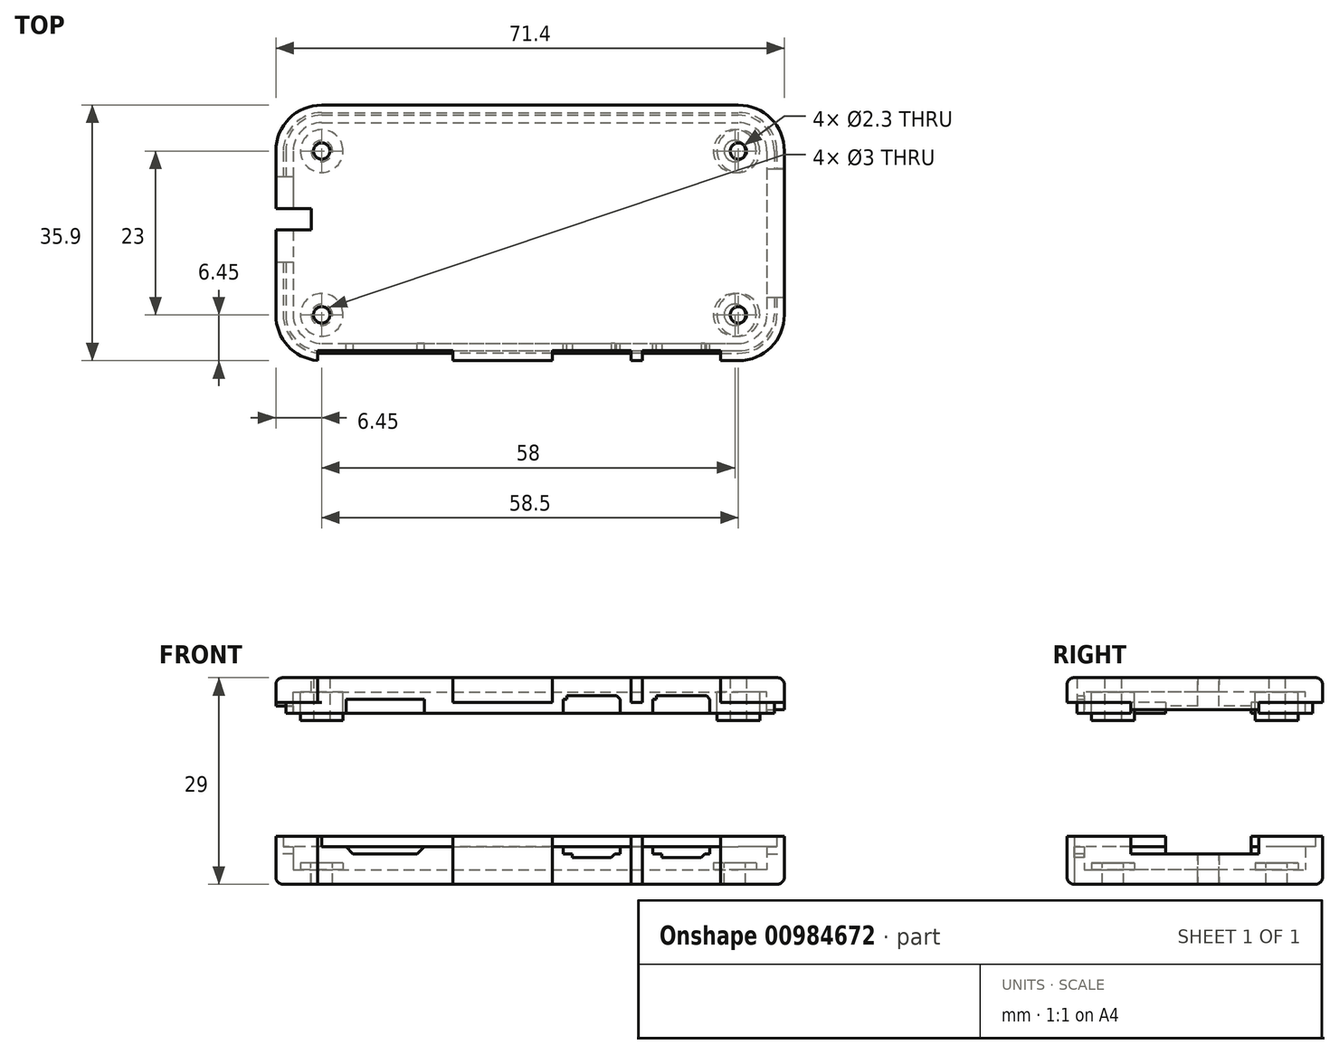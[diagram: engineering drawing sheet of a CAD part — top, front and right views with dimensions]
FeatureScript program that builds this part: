
annotation { "Feature Type Name" : "Feature", "Feature Type Description" : "" }
export const myFeature = defineFeature(function(context is Context, id is Id, definition is map)
    precondition{}
    {
        {
            var Q0;
            Q0=qCreatedBy(makeId("Top.planeOp"),FACE);
            var sketch = newSketch(context, id + "F0", { "sketchPlane" : qUnion([Q0])});
            skLineSegment(sketch, "E0.bottom", {"start": v(62, 30) * mm, "end": v(3, 30) * mm, "construction": true});
            skLineSegment(sketch, "E0.top", {"start": v(62, 0) * mm, "end": v(3, 0) * mm, "construction": true});
            skLineSegment(sketch, "E0.left", {"start": v(65, 27) * mm, "end": v(65, 3) * mm, "construction": true});
            skLineSegment(sketch, "E0.right", {"start": v(0, 27) * mm, "end": v(0, 3) * mm, "construction": true});
            skPoint(sketch, "E0.middle", {"position": v(32.5, 15) * mm});
            skLineSegment(sketch, "E1.bottom", {"start": v(61.5, 3.5) * mm, "end": v(3.5, 3.5) * mm, "construction": true});
            skLineSegment(sketch, "E1.top", {"start": v(61.5, 26.5) * mm, "end": v(3.5, 26.5) * mm, "construction": true});
            skLineSegment(sketch, "E1.left", {"start": v(61.5, 3.5) * mm, "end": v(61.5, 26.5) * mm, "construction": true});
            skLineSegment(sketch, "E1.right", {"start": v(3.5, 3.5) * mm, "end": v(3.5, 26.5) * mm, "construction": true});
            skPoint(sketch, "E2", {"position": v(0, 16.9) * mm});
            skPoint(sketch, "E3", {"position": v(12.4, 0) * mm});
            skPoint(sketch, "E4", {"position": v(41.4, 0) * mm});
            skPoint(sketch, "E5", {"position": v(54, 0) * mm});
            skPoint(sketch, "E6", {"position": v(65, 15) * mm});
            skPoint(sketch, "E7", {"position": v(32.5, 26.5) * mm});
            skLineSegment(sketch, "E8.bottom", {"start": v(58, 24) * mm, "end": v(7, 24) * mm, "construction": true});
            skLineSegment(sketch, "E8.top", {"start": v(58, 29) * mm, "end": v(7, 29) * mm, "construction": true});
            skLineSegment(sketch, "E8.left", {"start": v(58, 24) * mm, "end": v(58, 29) * mm, "construction": true});
            skLineSegment(sketch, "E8.right", {"start": v(7, 24) * mm, "end": v(7, 29) * mm, "construction": true});
            skLineSegment(sketch, "E9.bottom", {"start": v(50, 4) * mm, "end": v(58, 4) * mm, "construction": true});
            skLineSegment(sketch, "E9.top", {"start": v(50, -1.5) * mm, "end": v(58, -1.5) * mm, "construction": true});
            skLineSegment(sketch, "E9.left", {"start": v(50, 4) * mm, "end": v(50, -1.5) * mm, "construction": true});
            skLineSegment(sketch, "E9.right", {"start": v(58, 4) * mm, "end": v(58, -1.5) * mm, "construction": true});
            skLineSegment(sketch, "E10.bottom", {"start": v(37.4, 4) * mm, "end": v(45.4, 4) * mm, "construction": true});
            skLineSegment(sketch, "E10.top", {"start": v(37.4, -1.5) * mm, "end": v(45.4, -1.5) * mm, "construction": true});
            skLineSegment(sketch, "E10.left", {"start": v(37.4, 4) * mm, "end": v(37.4, -1.5) * mm, "construction": true});
            skLineSegment(sketch, "E10.right", {"start": v(45.4, 4) * mm, "end": v(45.4, -1.5) * mm, "construction": true});
            skLineSegment(sketch, "E11.bottom", {"start": v(6.9, 6.5) * mm, "end": v(17.9, 6.5) * mm, "construction": true});
            skLineSegment(sketch, "E11.top", {"start": v(6.9, -1) * mm, "end": v(17.9, -1) * mm, "construction": true});
            skLineSegment(sketch, "E11.left", {"start": v(6.9, 6.5) * mm, "end": v(6.9, -1) * mm, "construction": true});
            skLineSegment(sketch, "E11.right", {"start": v(17.9, 6.5) * mm, "end": v(17.9, -1) * mm, "construction": true});
            skLineSegment(sketch, "E12.bottom", {"start": v(-2.5, 22.9) * mm, "end": v(12.5, 22.9) * mm, "construction": true});
            skLineSegment(sketch, "E12.top", {"start": v(-2.5, 10.9) * mm, "end": v(12.5, 10.9) * mm, "construction": true});
            skLineSegment(sketch, "E12.left", {"start": v(-2.5, 22.9) * mm, "end": v(-2.5, 10.9) * mm, "construction": true});
            skLineSegment(sketch, "E12.right", {"start": v(12.5, 22.9) * mm, "end": v(12.5, 10.9) * mm, "construction": true});
            skLineSegment(sketch, "E13.bottom", {"start": v(61.25, 24) * mm, "end": v(65.5, 24) * mm, "construction": true});
            skLineSegment(sketch, "E13.top", {"start": v(61.25, 6) * mm, "end": v(65.5, 6) * mm, "construction": true});
            skLineSegment(sketch, "E13.left", {"start": v(61.25, 24) * mm, "end": v(61.25, 6) * mm, "construction": true});
            skLineSegment(sketch, "E13.right", {"start": v(65.5, 24) * mm, "end": v(65.5, 6) * mm, "construction": true});
            skLineSegment(sketch, "E14", {"start": v(65.5, 15) * mm, "end": v(61.25, 15) * mm, "construction": true});
            skLineSegment(sketch, "E15", {"start": v(54, 4) * mm, "end": v(54, -1.5) * mm, "construction": true});
            skLineSegment(sketch, "E16", {"start": v(41.4, 4) * mm, "end": v(41.4, -1.5) * mm, "construction": true});
            skLineSegment(sketch, "E17", {"start": v(12.4, 6.5) * mm, "end": v(12.4, -1) * mm, "construction": true});
            skLineSegment(sketch, "E18", {"start": v(12.5, 16.9) * mm, "end": v(-2.5, 16.9) * mm, "construction": true});
            skCircle(sketch, "E19", {"center": v(3.5, 26.5) * mm, "radius": 1.38 * mm, "construction": true});
            skCircle(sketch, "E20", {"center": v(3.5, 3.5) * mm, "radius": 1.38 * mm, "construction": true});
            skCircle(sketch, "E21", {"center": v(61.5, 26.5) * mm, "radius": 1.38 * mm, "construction": true});
            skCircle(sketch, "E22", {"center": v(61.5, 3.5) * mm, "radius": 1.38 * mm, "construction": true});
            skPoint(sketch, "E23.visualSharp", {"position": v(0, 30) * mm});
            skArc(sketch, "E23.filletArc", {"start": v(3, 30) * mm, "mid": v(0.88, 29.12) * mm, "end": v(0, 27) * mm, "construction": true});
            skPoint(sketch, "E24.visualSharp", {"position": v(0, 0) * mm});
            skArc(sketch, "E24.filletArc", {"start": v(0, 3) * mm, "mid": v(0.88, 0.88) * mm, "end": v(3, 0) * mm, "construction": true});
            skPoint(sketch, "E25.visualSharp", {"position": v(65, 30) * mm});
            skArc(sketch, "E25.filletArc", {"start": v(65, 27) * mm, "mid": v(64.12, 29.12) * mm, "end": v(62, 30) * mm, "construction": true});
            skPoint(sketch, "E26.visualSharp", {"position": v(65, 0) * mm});
            skArc(sketch, "E26.filletArc", {"start": v(62, 0) * mm, "mid": v(64.12, 0.88) * mm, "end": v(65, 3) * mm, "construction": true});
            skLineSegment(sketch, "E27.bottom", {"start": v(3.5, 30.5) * mm, "end": v(62, 30.5) * mm});
            skLineSegment(sketch, "E27.top", {"start": v(3.5, -0.5) * mm, "end": v(62, -0.5) * mm});
            skLineSegment(sketch, "E27.left", {"start": v(-0.5, 26.5) * mm, "end": v(-0.5, 3.5) * mm});
            skLineSegment(sketch, "E27.right", {"start": v(66, 26.5) * mm, "end": v(66, 3.5) * mm});
            skPoint(sketch, "E28.visualSharp", {"position": v(-0.5, 30.5) * mm});
            skArc(sketch, "E28.filletArc", {"start": v(3.5, 30.5) * mm, "mid": v(0.67, 29.33) * mm, "end": v(-0.5, 26.5) * mm});
            skPoint(sketch, "E29.visualSharp", {"position": v(66, 30.5) * mm});
            skArc(sketch, "E29.filletArc", {"start": v(66, 26.5) * mm, "mid": v(64.83, 29.33) * mm, "end": v(62, 30.5) * mm});
            skPoint(sketch, "E30.visualSharp", {"position": v(66, -0.5) * mm});
            skArc(sketch, "E30.filletArc", {"start": v(62, -0.5) * mm, "mid": v(64.83, 0.67) * mm, "end": v(66, 3.5) * mm});
            skPoint(sketch, "E31.visualSharp", {"position": v(-0.5, -0.5) * mm});
            skArc(sketch, "E31.filletArc", {"start": v(-0.5, 3.5) * mm, "mid": v(0.67, 0.67) * mm, "end": v(3.5, -0.5) * mm});
            skArc(sketch, "E32.0", {"start": v(3.5, 32.95) * mm, "mid": v(-1.06, 31.06) * mm, "end": v(-2.95, 26.5) * mm});
            skLineSegment(sketch, "E32.1", {"start": v(-2.95, 26.5) * mm, "end": v(-2.95, 3.5) * mm});
            skLineSegment(sketch, "E32.2", {"start": v(3.5, 32.95) * mm, "end": v(62, 32.95) * mm});
            skArc(sketch, "E32.3", {"start": v(-2.95, 3.5) * mm, "mid": v(-1.06, -1.06) * mm, "end": v(3.5, -2.95) * mm});
            skArc(sketch, "E32.4", {"start": v(68.45, 26.5) * mm, "mid": v(66.56, 31.06) * mm, "end": v(62, 32.95) * mm});
            skLineSegment(sketch, "E32.5", {"start": v(68.45, 26.5) * mm, "end": v(68.45, 3.5) * mm});
            skArc(sketch, "E32.6", {"start": v(62, -2.95) * mm, "mid": v(66.56, -1.06) * mm, "end": v(68.45, 3.5) * mm});
            skLineSegment(sketch, "E32.7", {"start": v(3.5, -2.95) * mm, "end": v(62, -2.95) * mm});
            skSolve(sketch);
        }
        {
            var Q0;
            Q0 = qSketchRegion(id + "F0", true);
            var Q1;
            Q1=makeQuery(id+"F0.imprint","IMPRINT",FACE,{"disambiguationData":[TD([[makeQuery(id+"F0.imprint","IMPRINT",EDGE,{"derivedFrom":sQuery(id+"F0.wireOp",EDGE,"E27.bottom")}),-1.0]])]});
            extrude(context, id + "F1", {"entities" : qUnion([Q0, Q1]), "oppositeDirection" : true, "depth" : 2 * mm, "offsetDistance" : 25 * mm});
        }
        {
            var Q0;
            Q0=makeQuery(id+"F0.imprint","IMPRINT",FACE,{"disambiguationData":[TD([[makeQuery(id+"F0.imprint","IMPRINT",EDGE,{"derivedFrom":sQuery(id+"F0.wireOp",EDGE,"E27.bottom")}),1.0]])]});
            extrude(context, id + "F2", {"entities" : qUnion([Q0]), "operationType" : NewBodyOperationType.ADD, "depth" : 3.25 * mm, "offsetDistance" : 25 * mm});
        }
        {
            var Q0;
            Q0=makeQuery(id+"F0.imprint","IMPRINT",FACE,{"disambiguationData":[TD([[makeQuery(id+"F0.imprint","IMPRINT",EDGE,{"derivedFrom":sQuery(id+"F0.wireOp",EDGE,"E27.bottom")}),-1.0]])]});
            var sketch = newSketch(context, id + "F3", { "sketchPlane" : qUnion([Q0])});
            skPoint(sketch, "E33.0", {"position": v(3.5, 26.5) * mm});
            skPoint(sketch, "E34.0", {"position": v(61.5, 26.5) * mm});
            skPoint(sketch, "E35.0", {"position": v(61.5, 3.5) * mm});
            skPoint(sketch, "E36.0", {"position": v(3.5, 3.5) * mm});
            skCircle(sketch, "E37", {"center": v(3.5, 26.5) * mm, "radius": 3 * mm});
            skCircle(sketch, "E38", {"center": v(61.5, 26.5) * mm, "radius": 3 * mm});
            skCircle(sketch, "E39", {"center": v(61.5, 3.5) * mm, "radius": 3 * mm});
            skCircle(sketch, "E40", {"center": v(3.5, 3.5) * mm, "radius": 3 * mm});
            skSolve(sketch);
        }
        {
            var Q0;
            Q0 = qSketchRegion(id + "F3", true);
            extrude(context, id + "F4", {"entities" : qUnion([Q0]), "operationType" : NewBodyOperationType.ADD, "depth" : 1 * mm, "offsetDistance" : 25 * mm});
        }
        {
            var Q0;
            Q0=makeQuery(id+"F0.imprint","IMPRINT",FACE,{"disambiguationData":[TD([[makeQuery(id+"F0.imprint","IMPRINT",EDGE,{"derivedFrom":sQuery(id+"F0.wireOp",EDGE,"E27.bottom")}),-1.0]])]});
            cPlane(context, id + "F5", {"entities" : qUnion([Q0]), "cplaneType" : CPlaneType.OFFSET, "offset" : 2.25 * mm, "width" : 150 * mm, "height" : 150 * mm});
        }
        {
            var Q0;
            Q0=qCreatedBy(id+"F5.planeOp",FACE);
            var sketch = newSketch(context, id + "F6", { "sketchPlane" : qUnion([Q0])});
            skLineSegment(sketch, "E41.bottom", {"start": v(-2.95, 22.9) * mm, "end": v(-0.5, 22.9) * mm});
            skLineSegment(sketch, "E41.top", {"start": v(-2.95, 10.9) * mm, "end": v(-0.5, 10.9) * mm});
            skLineSegment(sketch, "E41.left", {"start": v(-2.95, 22.9) * mm, "end": v(-2.95, 10.9) * mm});
            skLineSegment(sketch, "E41.right", {"start": v(-0.5, 22.9) * mm, "end": v(-0.5, 10.9) * mm});
            skLineSegment(sketch, "E42.bottom", {"start": v(6.9, -2.95) * mm, "end": v(17.9, -2.95) * mm});
            skLineSegment(sketch, "E42.top", {"start": v(6.9, -0.5) * mm, "end": v(17.9, -0.5) * mm});
            skLineSegment(sketch, "E42.left", {"start": v(6.9, -2.95) * mm, "end": v(6.9, -0.5) * mm});
            skLineSegment(sketch, "E42.right", {"start": v(17.9, -2.95) * mm, "end": v(17.9, -0.5) * mm});
            skLineSegment(sketch, "E43.bottom", {"start": v(37.4, -2.95) * mm, "end": v(45.4, -2.95) * mm});
            skLineSegment(sketch, "E43.top", {"start": v(37.4, -0.5) * mm, "end": v(45.4, -0.5) * mm});
            skLineSegment(sketch, "E43.left", {"start": v(37.4, -2.95) * mm, "end": v(37.4, -0.5) * mm});
            skLineSegment(sketch, "E43.right", {"start": v(45.4, -2.95) * mm, "end": v(45.4, -0.5) * mm});
            skLineSegment(sketch, "E44.bottom", {"start": v(50, -2.95) * mm, "end": v(58, -2.95) * mm});
            skLineSegment(sketch, "E44.top", {"start": v(50, -0.5) * mm, "end": v(58, -0.5) * mm});
            skLineSegment(sketch, "E44.left", {"start": v(50, -2.95) * mm, "end": v(50, -0.5) * mm});
            skLineSegment(sketch, "E44.right", {"start": v(58, -2.95) * mm, "end": v(58, -0.5) * mm});
            skLineSegment(sketch, "E45.bottom", {"start": v(66, 24) * mm, "end": v(68.45, 24) * mm});
            skLineSegment(sketch, "E45.top", {"start": v(66, 6) * mm, "end": v(68.45, 6) * mm});
            skLineSegment(sketch, "E45.left", {"start": v(66, 24) * mm, "end": v(66, 6) * mm});
            skLineSegment(sketch, "E45.right", {"start": v(68.45, 24) * mm, "end": v(68.45, 6) * mm});
            skSolve(sketch);
        }
        {
            var Q0;
            Q0 = qSketchRegion(id + "F6", true);
            var Q1;
            Q1=makeQuery(id+"F2.opExtrude","CAP_FACE",FACE,{"disambiguationData":[OSD([sQuery(id+"F0.wireOp",EDGE,"E27.bottom"),sQuery(id+"F0.wireOp",EDGE,"E27.top"),sQuery(id+"F0.wireOp",EDGE,"E27.left"),sQuery(id+"F0.wireOp",EDGE,"E27.right"),sQuery(id+"F0.wireOp",EDGE,"E28.filletArc"),sQuery(id+"F0.wireOp",EDGE,"E29.filletArc"),sQuery(id+"F0.wireOp",EDGE,"E30.filletArc"),sQuery(id+"F0.wireOp",EDGE,"E31.filletArc"),sQuery(id+"F0.wireOp",EDGE,"E32.0"),sQuery(id+"F0.wireOp",EDGE,"E32.1"),sQuery(id+"F0.wireOp",EDGE,"E32.2"),sQuery(id+"F0.wireOp",EDGE,"E32.3"),sQuery(id+"F0.wireOp",EDGE,"E32.4"),sQuery(id+"F0.wireOp",EDGE,"E32.5"),sQuery(id+"F0.wireOp",EDGE,"E32.6"),sQuery(id+"F0.wireOp",EDGE,"E32.7")])],"isStart":false});
            extrude(context, id + "F7", {"entities" : qUnion([Q0]), "operationType" : NewBodyOperationType.REMOVE, "endBound" : BoundingType.UP_TO_SURFACE, "depth" : 25 * mm, "endBoundEntityFace" : qUnion([Q1]), "offsetDistance" : 25 * mm});
        }
        {
            var Q0;
            Q0=qCreatedBy(makeId("Top.planeOp"),FACE);
            cPlane(context, id + "F8", {"entities" : qUnion([Q0]), "cplaneType" : CPlaneType.OFFSET, "offset" : 25 * mm, "width" : 150 * mm, "height" : 150 * mm});
        }
        {
            var Q0;
            Q0=qCreatedBy(id+"F8.planeOp",FACE);
            var sketch = newSketch(context, id + "F9", { "sketchPlane" : qUnion([Q0])});
            skLineSegment(sketch, "E46.0", {"start": v(3.5, 32.95) * mm, "end": v(62, 32.95) * mm});
            skArc(sketch, "E47.0", {"start": v(3.5, 32.95) * mm, "mid": v(-1.06, 31.06) * mm, "end": v(-2.95, 26.5) * mm});
            skLineSegment(sketch, "E48.0", {"start": v(-2.95, 26.5) * mm, "end": v(-2.95, 3.5) * mm});
            skArc(sketch, "E49.0", {"start": v(-2.95, 3.5) * mm, "mid": v(-1.06, -1.06) * mm, "end": v(3.5, -2.95) * mm});
            skLineSegment(sketch, "E50.0", {"start": v(3.5, -2.95) * mm, "end": v(62, -2.95) * mm});
            skArc(sketch, "E51.0", {"start": v(62, -2.95) * mm, "mid": v(66.56, -1.06) * mm, "end": v(68.45, 3.5) * mm});
            skLineSegment(sketch, "E52.0", {"start": v(68.45, 26.5) * mm, "end": v(68.45, 3.5) * mm});
            skArc(sketch, "E53.0", {"start": v(68.45, 26.5) * mm, "mid": v(66.56, 31.06) * mm, "end": v(62, 32.95) * mm});
            skLineSegment(sketch, "E54.0", {"start": v(3.5, -0.5) * mm, "end": v(62, -0.5) * mm});
            skArc(sketch, "E55.0", {"start": v(62, -0.5) * mm, "mid": v(64.83, 0.67) * mm, "end": v(66, 3.5) * mm});
            skLineSegment(sketch, "E56.0", {"start": v(66, 26.5) * mm, "end": v(66, 3.5) * mm});
            skArc(sketch, "E57.0", {"start": v(66, 26.5) * mm, "mid": v(64.83, 29.33) * mm, "end": v(62, 30.5) * mm});
            skLineSegment(sketch, "E58.0", {"start": v(3.5, 30.5) * mm, "end": v(62, 30.5) * mm});
            skArc(sketch, "E59.0", {"start": v(3.5, 30.5) * mm, "mid": v(0.67, 29.33) * mm, "end": v(-0.5, 26.5) * mm});
            skLineSegment(sketch, "E60.0", {"start": v(-0.5, 26.5) * mm, "end": v(-0.5, 3.5) * mm});
            skArc(sketch, "E61.0", {"start": v(-0.5, 3.5) * mm, "mid": v(0.67, 0.67) * mm, "end": v(3.5, -0.5) * mm});
            skSolve(sketch);
        }
        {
            var Q0;
            Q0 = qSketchRegion(id + "F9", true);
            var Q1;
            Q1=makeQuery(id+"F9.imprint","IMPRINT",FACE,{"disambiguationData":[TD([[makeQuery(id+"F9.imprint","IMPRINT",EDGE,{"derivedFrom":sQuery(id+"F9.wireOp",EDGE,"E54.0")}),1.0]])]});
            extrude(context, id + "F10", {"entities" : qUnion([Q0, Q1]), "depth" : 2 * mm, "offsetDistance" : 25 * mm});
        }
        {
            var Q0;
            Q0=makeQuery(id+"F9.imprint","IMPRINT",FACE,{"disambiguationData":[TD([[makeQuery(id+"F9.imprint","IMPRINT",EDGE,{"derivedFrom":sQuery(id+"F9.wireOp",EDGE,"E46.0")}),-1.0]])]});
            extrude(context, id + "F11", {"entities" : qUnion([Q0]), "operationType" : NewBodyOperationType.ADD, "oppositeDirection" : true, "depth" : 3 * mm, "offsetDistance" : 25 * mm});
        }
        {
            var Q0;
            Q0=makeQuery(id+"F11.opExtrude","CAP_FACE",FACE,{"disambiguationData":[OSD([sQuery(id+"F9.wireOp",EDGE,"E46.0"),sQuery(id+"F9.wireOp",EDGE,"E47.0"),sQuery(id+"F9.wireOp",EDGE,"E48.0"),sQuery(id+"F9.wireOp",EDGE,"E49.0"),sQuery(id+"F9.wireOp",EDGE,"E50.0"),sQuery(id+"F9.wireOp",EDGE,"E51.0"),sQuery(id+"F9.wireOp",EDGE,"E52.0"),sQuery(id+"F9.wireOp",EDGE,"E53.0"),sQuery(id+"F9.wireOp",EDGE,"E54.0"),sQuery(id+"F9.wireOp",EDGE,"E55.0"),sQuery(id+"F9.wireOp",EDGE,"E56.0"),sQuery(id+"F9.wireOp",EDGE,"E57.0"),sQuery(id+"F9.wireOp",EDGE,"E58.0"),sQuery(id+"F9.wireOp",EDGE,"E59.0"),sQuery(id+"F9.wireOp",EDGE,"E60.0"),sQuery(id+"F9.wireOp",EDGE,"E61.0")])],"isStart":false});
            var sketch = newSketch(context, id + "F12", { "sketchPlane" : qUnion([Q0])});
            skLineSegment(sketch, "E62.0", {"start": v(66, -24) * mm, "end": v(68.45, -24) * mm});
            skLineSegment(sketch, "E63.0", {"start": v(66, -6) * mm, "end": v(68.45, -6) * mm});
            skLineSegment(sketch, "E64.0", {"start": v(66, -24) * mm, "end": v(66, -6) * mm});
            skLineSegment(sketch, "E65.0", {"start": v(68.45, -24) * mm, "end": v(68.45, -6) * mm});
            skLineSegment(sketch, "E66.0", {"start": v(50, 2.95) * mm, "end": v(50, 0.5) * mm});
            skLineSegment(sketch, "E67.0", {"start": v(50, 2.95) * mm, "end": v(58, 2.95) * mm});
            skLineSegment(sketch, "E68.0", {"start": v(50, 0.5) * mm, "end": v(58, 0.5) * mm});
            skLineSegment(sketch, "E69.0", {"start": v(58, 2.95) * mm, "end": v(58, 0.5) * mm});
            skLineSegment(sketch, "E70.0", {"start": v(45.4, 2.95) * mm, "end": v(45.4, 0.5) * mm});
            skLineSegment(sketch, "E71.0", {"start": v(37.4, 0.5) * mm, "end": v(45.4, 0.5) * mm});
            skLineSegment(sketch, "E72.0", {"start": v(37.4, 2.95) * mm, "end": v(45.4, 2.95) * mm});
            skLineSegment(sketch, "E73.0", {"start": v(37.4, 2.95) * mm, "end": v(37.4, 0.5) * mm});
            skLineSegment(sketch, "E74.0", {"start": v(6.9, 2.95) * mm, "end": v(6.9, 0.5) * mm});
            skLineSegment(sketch, "E75.0", {"start": v(6.9, 2.95) * mm, "end": v(17.9, 2.95) * mm});
            skLineSegment(sketch, "E76.0", {"start": v(6.9, 0.5) * mm, "end": v(17.9, 0.5) * mm});
            skLineSegment(sketch, "E77.0", {"start": v(17.9, 2.95) * mm, "end": v(17.9, 0.5) * mm});
            skLineSegment(sketch, "E78.0", {"start": v(-2.95, -10.9) * mm, "end": v(-0.5, -10.9) * mm});
            skLineSegment(sketch, "E79.0", {"start": v(-2.95, -22.9) * mm, "end": v(-0.5, -22.9) * mm});
            skLineSegment(sketch, "E80.0", {"start": v(-0.5, -22.9) * mm, "end": v(-0.5, -10.9) * mm});
            skLineSegment(sketch, "E81.0", {"start": v(-2.95, -22.9) * mm, "end": v(-2.95, -10.9) * mm});
            skSolve(sketch);
        }
        {
            var Q0;
            Q0=makeQuery(id+"F12.imprint","IMPRINT",FACE,{"disambiguationData":[TD([[makeQuery(id+"F12.imprint","IMPRINT",EDGE,{"derivedFrom":sQuery(id+"F12.wireOp",EDGE,"E78.0")}),-1.0]])]});
            extrude(context, id + "F13", {"entities" : qUnion([Q0]), "operationType" : NewBodyOperationType.REMOVE, "oppositeDirection" : true, "depth" : 1 * mm, "offsetDistance" : 25 * mm});
        }
        {
            var Q0;
            Q0=makeQuery(id+"F12.imprint","IMPRINT",FACE,{"disambiguationData":[TD([[makeQuery(id+"F12.imprint","IMPRINT",EDGE,{"derivedFrom":sQuery(id+"F12.wireOp",EDGE,"E74.0")}),1.0]])]});
            extrude(context, id + "F14", {"entities" : qUnion([Q0]), "operationType" : NewBodyOperationType.REMOVE, "oppositeDirection" : true, "depth" : 2 * mm, "offsetDistance" : 25 * mm});
        }
        {
            var Q0;
            Q0=makeQuery(id+"F12.imprint","IMPRINT",FACE,{"disambiguationData":[TD([[makeQuery(id+"F12.imprint","IMPRINT",EDGE,{"derivedFrom":sQuery(id+"F12.wireOp",EDGE,"E70.0")}),-1.0]])]});
            var Q1;
            Q1=makeQuery(id+"F12.imprint","IMPRINT",FACE,{"disambiguationData":[TD([[makeQuery(id+"F12.imprint","IMPRINT",EDGE,{"derivedFrom":sQuery(id+"F12.wireOp",EDGE,"E66.0")}),1.0]])]});
            extrude(context, id + "F15", {"entities" : qUnion([Q0, Q1]), "operationType" : NewBodyOperationType.REMOVE, "oppositeDirection" : true, "depth" : 2 * mm, "offsetDistance" : 25 * mm});
        }
        {
            var Q0;
            Q0=makeQuery(id+"F12.imprint","IMPRINT",FACE,{"disambiguationData":[TD([[makeQuery(id+"F12.imprint","IMPRINT",EDGE,{"derivedFrom":sQuery(id+"F12.wireOp",EDGE,"E62.0")}),1.0]])]});
            extrude(context, id + "F16", {"entities" : qUnion([Q0]), "operationType" : NewBodyOperationType.REMOVE, "oppositeDirection" : true, "depth" : 0.5 * mm, "offsetDistance" : 25 * mm});
        }
        {
            var Q0;
            Q0=qCreatedBy(id+"F8.planeOp",FACE);
            var sketch = newSketch(context, id + "F17", { "sketchPlane" : qUnion([Q0])});
            skPoint(sketch, "E82.0", {"position": v(3.5, 3.5) * mm});
            skPoint(sketch, "E83.0", {"position": v(3.5, 26.5) * mm});
            skPoint(sketch, "E84.0", {"position": v(62, 26.5) * mm});
            skPoint(sketch, "E85.0", {"position": v(62, 3.5) * mm});
            skCircle(sketch, "E86", {"center": v(3.5, 26.5) * mm, "radius": 3 * mm});
            skCircle(sketch, "E87", {"center": v(3.5, 3.5) * mm, "radius": 3 * mm});
            skCircle(sketch, "E88", {"center": v(62, 3.5) * mm, "radius": 3 * mm});
            skCircle(sketch, "E89", {"center": v(62, 26.5) * mm, "radius": 3 * mm});
            skSolve(sketch);
        }
        {
            var Q0;
            Q0 = qSketchRegion(id + "F17", true);
            extrude(context, id + "F18", {"entities" : qUnion([Q0]), "operationType" : NewBodyOperationType.ADD, "oppositeDirection" : true, "depth" : 4 * mm, "offsetDistance" : 25 * mm});
        }
        {
            var Q0;
            Q0=makeQuery(id+"F18.opExtrude","CAP_FACE",FACE,{"disambiguationData":[OSD([sQuery(id+"F17.wireOp",EDGE,"E86")])],"isStart":false});
            var sketch = newSketch(context, id + "F19", { "sketchPlane" : qUnion([Q0])});
            skPoint(sketch, "E90.0", {"position": v(3.5, -26.5) * mm});
            skPoint(sketch, "E91.0", {"position": v(3.5, -3.5) * mm});
            skPoint(sketch, "E92.0", {"position": v(62, -26.5) * mm});
            skPoint(sketch, "E93.0", {"position": v(62, -3.5) * mm});
            skSolve(sketch);
        }
        {
            var Q0;
            Q0=sQuery(id+"F19.wireOp",VERTEX,"E92.0");
            var Q1;
            Q1=sQuery(id+"F19.wireOp",VERTEX,"E93.0");
            var Q2;
            Q2=sQuery(id+"F19.wireOp",VERTEX,"E91.0");
            var Q3;
            Q3=sQuery(id+"F19.wireOp",VERTEX,"E90.0");
            var Q4;
            Q4=makeQuery(id+"F10.opExtrude","SWEPT_BODY",BODY,{"disambiguationData":[OSD([sQuery(id+"F9.wireOp",EDGE,"E46.0"),sQuery(id+"F9.wireOp",EDGE,"E47.0"),sQuery(id+"F9.wireOp",EDGE,"E48.0"),sQuery(id+"F9.wireOp",EDGE,"E49.0"),sQuery(id+"F9.wireOp",EDGE,"E50.0"),sQuery(id+"F9.wireOp",EDGE,"E51.0"),sQuery(id+"F9.wireOp",EDGE,"E52.0"),sQuery(id+"F9.wireOp",EDGE,"E53.0")])]});
            hole(context, id + "F20", {"style" : HoleStyle.SIMPLE, "endStyle" : HoleEndStyle.BLIND, "holeDiameter" : 2.3 * mm, "majorDiameter" : 5 * mm, "holeDepth" : 13 * mm, "isTappedThrough" : true, "tappedDepth" : 12 * mm, "tapClearance" : 3, "locations" : qUnion([Q0, Q1, Q2, Q3]), "scope" : qUnion([Q4])});
        }
        {
            var Q0;
            Q0=makeQuery(id+"F4.opExtrude","CAP_FACE",FACE,{"disambiguationData":[OSD([sQuery(id+"F3.wireOp",EDGE,"E37")])],"isStart":false});
            var sketch = newSketch(context, id + "F21", { "sketchPlane" : qUnion([Q0])});
            skPoint(sketch, "E94.0", {"position": v(3.5, 26.5) * mm});
            skPoint(sketch, "E95.0", {"position": v(3.5, 3.5) * mm});
            skPoint(sketch, "E96.0", {"position": v(61.5, 26.5) * mm});
            skPoint(sketch, "E97.0", {"position": v(61.5, 3.5) * mm});
            skSolve(sketch);
        }
        {
            var Q0;
            Q0=sQuery(id+"F21.wireOp",VERTEX,"E96.0");
            var Q1;
            Q1=sQuery(id+"F21.wireOp",VERTEX,"E97.0");
            var Q2;
            Q2=sQuery(id+"F21.wireOp",VERTEX,"E95.0");
            var Q3;
            Q3=sQuery(id+"F21.wireOp",VERTEX,"E94.0");
            var Q4;
            Q4=makeQuery(id+"F1.opExtrude","SWEPT_BODY",BODY,{"disambiguationData":[OSD([sQuery(id+"F0.wireOp",EDGE,"E32.0"),sQuery(id+"F0.wireOp",EDGE,"E32.1"),sQuery(id+"F0.wireOp",EDGE,"E32.2"),sQuery(id+"F0.wireOp",EDGE,"E32.3"),sQuery(id+"F0.wireOp",EDGE,"E32.4"),sQuery(id+"F0.wireOp",EDGE,"E32.5"),sQuery(id+"F0.wireOp",EDGE,"E32.6"),sQuery(id+"F0.wireOp",EDGE,"E32.7")])]});
            hole(context, id + "F22", {"style" : HoleStyle.SIMPLE, "endStyle" : HoleEndStyle.BLIND, "holeDiameter" : 3 * mm, "majorDiameter" : 5 * mm, "holeDepth" : 13 * mm, "isTappedThrough" : true, "tappedDepth" : 12 * mm, "tapClearance" : 3, "locations" : qUnion([Q0, Q1, Q2, Q3]), "scope" : qUnion([Q4])});
        }
        {
            var Q0;
            {var subQ0=sQuery(id+"F0.wireOp",EDGE,"E32.1");Q0=makeQuery(id+"F2.boolean.opBoolean","MERGE",FACE,{"derivedFrom":[makeQuery(id+"F1.opExtrude","SWEPT_FACE",FACE,{"disambiguationData":[OSD([subQ0])]}),makeQuery(id+"F2.opExtrude","SWEPT_FACE",FACE,{"disambiguationData":[OSD([subQ0])]})]});}
            var sketch = newSketch(context, id + "F23", { "sketchPlane" : qUnion([Q0])});
            skLineSegment(sketch, "E98", {"start": v(-16.9, 2.25) * mm, "end": v(-16.9, -2) * mm, "construction": true});
            skLineSegment(sketch, "E99.bottom", {"start": v(-15.4, -2) * mm, "end": v(-18.4, -2) * mm});
            skLineSegment(sketch, "E99.top", {"start": v(-15.4, 2.25) * mm, "end": v(-18.4, 2.25) * mm});
            skLineSegment(sketch, "E99.left", {"start": v(-15.4, -2) * mm, "end": v(-15.4, 2.25) * mm});
            skLineSegment(sketch, "E99.right", {"start": v(-18.4, -2) * mm, "end": v(-18.4, 2.25) * mm});
            skPoint(sketch, "E99.middle", {"position": v(-16.9, 0.13) * mm});
            skSolve(sketch);
        }
        {
            var Q0;
            Q0 = qSketchRegion(id + "F23", true);
            extrude(context, id + "F24", {"entities" : qUnion([Q0]), "operationType" : NewBodyOperationType.REMOVE, "oppositeDirection" : true, "depth" : 5 * mm, "offsetDistance" : 25 * mm});
        }
        {
            var Q0;
            {var subQ0=sQuery(id+"F9.wireOp",EDGE,"E48.0");Q0=makeQuery(id+"F11.boolean.opBoolean","MERGE",FACE,{"derivedFrom":[makeQuery(id+"F10.opExtrude","SWEPT_FACE",FACE,{"disambiguationData":[OSD([subQ0])]}),makeQuery(id+"F11.opExtrude","SWEPT_FACE",FACE,{"disambiguationData":[OSD([subQ0])]})]});}
            var sketch = newSketch(context, id + "F25", { "sketchPlane" : qUnion([Q0])});
            skLineSegment(sketch, "E100", {"start": v(-16.9, 23) * mm, "end": v(-16.9, 27) * mm, "construction": true});
            skLineSegment(sketch, "E101.bottom", {"start": v(-15.4, 23) * mm, "end": v(-18.4, 23) * mm});
            skLineSegment(sketch, "E101.top", {"start": v(-15.4, 27) * mm, "end": v(-18.4, 27) * mm});
            skLineSegment(sketch, "E101.left", {"start": v(-15.4, 23) * mm, "end": v(-15.4, 27) * mm});
            skLineSegment(sketch, "E101.right", {"start": v(-18.4, 23) * mm, "end": v(-18.4, 27) * mm});
            skPoint(sketch, "E101.middle", {"position": v(-16.9, 25) * mm});
            skSolve(sketch);
        }
        {
            var Q0;
            Q0=makeQuery(id+"F25.imprint","IMPRINT",FACE,{"disambiguationData":[TD([[makeQuery(id+"F25.imprint","IMPRINT",EDGE,{"derivedFrom":sQuery(id+"F25.wireOp",EDGE,"E101.bottom")}),1.0]])]});
            extrude(context, id + "F26", {"entities" : qUnion([Q0]), "operationType" : NewBodyOperationType.REMOVE, "oppositeDirection" : true, "depth" : 5 * mm, "offsetDistance" : 25 * mm});
        }
        {
            var Q0;
            Q0=makeQuery(id+"F10.opExtrude","CAP_EDGE",EDGE,{"disambiguationData":[OSD([sQuery(id+"F9.wireOp",EDGE,"E50.0")])],"isStart":false});
            var Q1;
            Q1=makeQuery(id+"F1.opExtrude","CAP_EDGE",EDGE,{"disambiguationData":[OSD([sQuery(id+"F0.wireOp",EDGE,"E32.6")])],"isStart":false});
            fillet(context, id + "F27", {"entities" : qUnion([Q0, Q1]), "radius" : 1 * mm, "tangentPropagation" : true, "allowEdgeOverflow" : false});
        }
        {
            var Q0;
            Q0=makeQuery(id+"F6.imprint","IMPRINT",FACE,{"disambiguationData":[TD([[makeQuery(id+"F6.imprint","IMPRINT",EDGE,{"derivedFrom":sQuery(id+"F6.wireOp",EDGE,"E43.bottom")}),1.0]])]});
            var sketch = newSketch(context, id + "F28", { "sketchPlane" : qUnion([Q0])});
            skLineSegment(sketch, "E102.bottom", {"start": v(38.65, -0.5) * mm, "end": v(44.15, -0.5) * mm});
            skLineSegment(sketch, "E102.top", {"start": v(38.65, -2.95) * mm, "end": v(44.15, -2.95) * mm});
            skLineSegment(sketch, "E102.left", {"start": v(38.65, -0.5) * mm, "end": v(38.65, -2.95) * mm});
            skLineSegment(sketch, "E102.right", {"start": v(44.15, -0.5) * mm, "end": v(44.15, -2.95) * mm});
            skLineSegment(sketch, "E103.bottom", {"start": v(51.25, -0.5) * mm, "end": v(56.75, -0.5) * mm});
            skLineSegment(sketch, "E103.top", {"start": v(51.25, -2.95) * mm, "end": v(56.75, -2.95) * mm});
            skLineSegment(sketch, "E103.left", {"start": v(51.25, -0.5) * mm, "end": v(51.25, -2.95) * mm});
            skLineSegment(sketch, "E103.right", {"start": v(56.75, -0.5) * mm, "end": v(56.75, -2.95) * mm});
            skLineSegment(sketch, "E104", {"start": v(41.4, -0.5) * mm, "end": v(41.4, -2.95) * mm, "construction": true});
            skLineSegment(sketch, "E105", {"start": v(54, -0.5) * mm, "end": v(54, -2.95) * mm, "construction": true});
            skSolve(sketch);
        }
        {
            var Q0;
            Q0 = qSketchRegion(id + "F28", true);
            extrude(context, id + "F29", {"entities" : qUnion([Q0]), "operationType" : NewBodyOperationType.REMOVE, "oppositeDirection" : true, "depth" : 0.5 * mm, "offsetDistance" : 25 * mm});
        }
        {
            var Q0;
            Q0=makeQuery(id+"F29.boolean.opBoolean","COPY",EDGE,{"derivedFrom":makeQuery(id+"F29.opExtrude","CAP_EDGE",EDGE,{"disambiguationData":[OSD([sQuery(id+"F28.wireOp",EDGE,"E102.right")])],"isStart":true})});
            var Q1;
            Q1=makeQuery(id+"F29.boolean.opBoolean","COPY",EDGE,{"derivedFrom":makeQuery(id+"F29.opExtrude","CAP_EDGE",EDGE,{"disambiguationData":[OSD([sQuery(id+"F28.wireOp",EDGE,"E102.left")])],"isStart":true})});
            var Q2;
            Q2=makeQuery(id+"F29.boolean.opBoolean","COPY",EDGE,{"derivedFrom":makeQuery(id+"F29.opExtrude","CAP_EDGE",EDGE,{"disambiguationData":[OSD([sQuery(id+"F28.wireOp",EDGE,"E103.left")])],"isStart":true})});
            var Q3;
            Q3=makeQuery(id+"F29.boolean.opBoolean","COPY",EDGE,{"derivedFrom":makeQuery(id+"F29.opExtrude","CAP_EDGE",EDGE,{"disambiguationData":[OSD([sQuery(id+"F28.wireOp",EDGE,"E103.right")])],"isStart":true})});
            chamfer(context, id + "F30", {"entities" : qUnion([Q0, Q1, Q2, Q3]), "width" : 0.5 * mm, "tangentPropagation" : true});
        }
        {
            var Q0;
            Q0=makeQuery(id+"F15.boolean.opBoolean","COPY",FACE,{"derivedFrom":makeQuery(id+"F15.opExtrude","CAP_FACE",FACE,{"disambiguationData":[OSD([sQuery(id+"F12.wireOp",EDGE,"E70.0"),sQuery(id+"F12.wireOp",EDGE,"E71.0"),sQuery(id+"F12.wireOp",EDGE,"E72.0"),sQuery(id+"F12.wireOp",EDGE,"E73.0")])],"isStart":false})});
            var sketch = newSketch(context, id + "F31", { "sketchPlane" : qUnion([Q0])});
            skLineSegment(sketch, "E106.bottom", {"start": v(37.9, 2.95) * mm, "end": v(44.9, 2.95) * mm});
            skLineSegment(sketch, "E106.top", {"start": v(37.9, 0.5) * mm, "end": v(44.9, 0.5) * mm});
            skLineSegment(sketch, "E106.left", {"start": v(37.9, 2.95) * mm, "end": v(37.9, 0.5) * mm});
            skLineSegment(sketch, "E106.right", {"start": v(44.9, 2.95) * mm, "end": v(44.9, 0.5) * mm});
            skLineSegment(sketch, "E107.bottom", {"start": v(50.5, 2.95) * mm, "end": v(57.5, 2.95) * mm});
            skLineSegment(sketch, "E107.top", {"start": v(50.5, 0.5) * mm, "end": v(57.5, 0.5) * mm});
            skLineSegment(sketch, "E107.left", {"start": v(50.5, 2.95) * mm, "end": v(50.5, 0.5) * mm});
            skLineSegment(sketch, "E107.right", {"start": v(57.5, 2.95) * mm, "end": v(57.5, 0.5) * mm});
            skLineSegment(sketch, "E108", {"start": v(41.4, 2.95) * mm, "end": v(41.4, 0.5) * mm, "construction": true});
            skLineSegment(sketch, "E109", {"start": v(54, 2.95) * mm, "end": v(54, 0.5) * mm, "construction": true});
            skLineSegment(sketch, "E110", {"start": v(54, 0.5) * mm, "end": v(54.12, 0.44) * mm, "construction": true});
            skSolve(sketch);
        }
        {
            var Q0;
            Q0=makeQuery(id+"F31.imprint","IMPRINT",FACE,{"disambiguationData":[TD([[makeQuery(id+"F31.imprint","IMPRINT",EDGE,{"derivedFrom":sQuery(id+"F31.wireOp",EDGE,"E106.bottom")}),-1.0]])]});
            var Q1;
            Q1=makeQuery(id+"F31.imprint","IMPRINT",FACE,{"disambiguationData":[TD([[makeQuery(id+"F31.imprint","IMPRINT",EDGE,{"derivedFrom":sQuery(id+"F31.wireOp",EDGE,"E107.bottom")}),-1.0]])]});
            extrude(context, id + "F32", {"entities" : qUnion([Q0, Q1]), "operationType" : NewBodyOperationType.REMOVE, "oppositeDirection" : true, "depth" : 0.5 * mm, "offsetDistance" : 25 * mm});
        }
        {
            var Q0;
            Q0=makeQuery(id+"F32.boolean.opBoolean","COPY",EDGE,{"derivedFrom":makeQuery(id+"F32.opExtrude","CAP_EDGE",EDGE,{"disambiguationData":[OSD([sQuery(id+"F31.wireOp",EDGE,"E106.right")])],"isStart":true})});
            var Q1;
            Q1=makeQuery(id+"F32.boolean.opBoolean","COPY",EDGE,{"derivedFrom":makeQuery(id+"F32.opExtrude","CAP_EDGE",EDGE,{"disambiguationData":[OSD([sQuery(id+"F31.wireOp",EDGE,"E107.right")])],"isStart":true})});
            var Q2;
            Q2=makeQuery(id+"F32.boolean.opBoolean","COPY",EDGE,{"derivedFrom":makeQuery(id+"F32.opExtrude","CAP_EDGE",EDGE,{"disambiguationData":[OSD([sQuery(id+"F31.wireOp",EDGE,"E107.left")])],"isStart":true})});
            var Q3;
            Q3=makeQuery(id+"F32.boolean.opBoolean","COPY",EDGE,{"derivedFrom":makeQuery(id+"F32.opExtrude","CAP_EDGE",EDGE,{"disambiguationData":[OSD([sQuery(id+"F31.wireOp",EDGE,"E106.left")])],"isStart":true})});
            chamfer(context, id + "F33", {"entities" : qUnion([Q0, Q1, Q2, Q3]), "width" : 0.5 * mm, "tangentPropagation" : true});
        }
        {
            var Q0;
            {var subQ3=sQuery(id+"F12.wireOp",EDGE,"E74.0");Q0=makeQuery(id+"F12.imprint","IMPRINT",FACE,{"disambiguationData":[TD([[makeQuery(id+"F12.imprint","IMPRINT",EDGE,{"derivedFrom":subQ3}),-1.0]])]});}
            var sketch = newSketch(context, id + "F34", { "sketchPlane" : qUnion([Q0])});
            skLineSegment(sketch, "E111.0", {"start": v(3.5, 1.55) * mm, "end": v(6.9, 1.55) * mm});
            skArc(sketch, "E111.1", {"start": v(-1.55, -3.5) * mm, "mid": v(-0.07, 0.07) * mm, "end": v(3.5, 1.55) * mm});
            skLineSegment(sketch, "E111.2", {"start": v(-1.55, -10.9) * mm, "end": v(-1.55, -3.5) * mm});
            skLineSegment(sketch, "E112", {"start": v(6.9, 1.55) * mm, "end": v(6.9, 2.95) * mm});
            skLineSegment(sketch, "E113", {"start": v(-1.55, -10.9) * mm, "end": v(-2.95, -10.9) * mm});
            skLineSegment(sketch, "E114.bottom", {"start": v(17.9, 2.95) * mm, "end": v(37.4, 2.95) * mm});
            skLineSegment(sketch, "E114.top", {"start": v(17.9, 1.55) * mm, "end": v(37.4, 1.55) * mm});
            skLineSegment(sketch, "E114.left", {"start": v(17.9, 2.95) * mm, "end": v(17.9, 1.55) * mm});
            skLineSegment(sketch, "E114.right", {"start": v(37.4, 2.95) * mm, "end": v(37.4, 1.55) * mm});
            skLineSegment(sketch, "E115.bottom", {"start": v(45.4, 2.95) * mm, "end": v(50, 2.95) * mm});
            skLineSegment(sketch, "E115.top", {"start": v(45.4, 1.55) * mm, "end": v(50, 1.55) * mm});
            skLineSegment(sketch, "E115.left", {"start": v(45.4, 2.95) * mm, "end": v(45.4, 1.55) * mm});
            skLineSegment(sketch, "E115.right", {"start": v(50, 2.95) * mm, "end": v(50, 1.55) * mm});
            skLineSegment(sketch, "E116.0", {"start": v(67.05, -6) * mm, "end": v(67.05, -3.5) * mm});
            skArc(sketch, "E116.1", {"start": v(62, 1.55) * mm, "mid": v(65.57, 0.07) * mm, "end": v(67.05, -3.5) * mm});
            skLineSegment(sketch, "E116.2", {"start": v(58, 1.55) * mm, "end": v(62, 1.55) * mm});
            skLineSegment(sketch, "E117", {"start": v(58, 1.55) * mm, "end": v(58, 2.95) * mm});
            skLineSegment(sketch, "E118", {"start": v(67.05, -6) * mm, "end": v(68.45, -6) * mm});
            skLineSegment(sketch, "E119.0", {"start": v(67.05, -26.5) * mm, "end": v(67.05, -24) * mm});
            skLineSegment(sketch, "E119.1", {"start": v(-1.55, -26.5) * mm, "end": v(-1.55, -22.9) * mm});
            skArc(sketch, "E119.2", {"start": v(3.5, -31.55) * mm, "mid": v(-0.07, -30.07) * mm, "end": v(-1.55, -26.5) * mm});
            skLineSegment(sketch, "E119.3", {"start": v(3.5, -31.55) * mm, "end": v(62, -31.55) * mm});
            skArc(sketch, "E119.4", {"start": v(67.05, -26.5) * mm, "mid": v(65.57, -30.07) * mm, "end": v(62, -31.55) * mm});
            skLineSegment(sketch, "E120", {"start": v(67.05, -24) * mm, "end": v(68.45, -24) * mm});
            skLineSegment(sketch, "E121", {"start": v(-1.55, -22.9) * mm, "end": v(-2.95, -22.9) * mm});
            skLineSegment(sketch, "E122.0", {"start": v(-2.95, -26.5) * mm, "end": v(-2.95, -22.9) * mm});
            skArc(sketch, "E123.0", {"start": v(3.5, -32.95) * mm, "mid": v(-1.06, -31.06) * mm, "end": v(-2.95, -26.5) * mm});
            skLineSegment(sketch, "E124.0", {"start": v(3.5, -32.95) * mm, "end": v(62, -32.95) * mm});
            skArc(sketch, "E125.0", {"start": v(68.45, -26.5) * mm, "mid": v(66.56, -31.06) * mm, "end": v(62, -32.95) * mm});
            skLineSegment(sketch, "E126.0", {"start": v(68.45, -26.5) * mm, "end": v(68.45, -24) * mm});
            skLineSegment(sketch, "E127.0", {"start": v(68.45, -6) * mm, "end": v(68.45, -3.5) * mm});
            skArc(sketch, "E128.0", {"start": v(62, 2.95) * mm, "mid": v(66.56, 1.06) * mm, "end": v(68.45, -3.5) * mm});
            skLineSegment(sketch, "E129.0", {"start": v(58, 2.95) * mm, "end": v(62, 2.95) * mm});
            skLineSegment(sketch, "E130.0", {"start": v(3.5, 2.95) * mm, "end": v(6.9, 2.95) * mm});
            skArc(sketch, "E131.0", {"start": v(-2.95, -3.5) * mm, "mid": v(-1.06, 1.06) * mm, "end": v(3.5, 2.95) * mm});
            skLineSegment(sketch, "E132.0", {"start": v(-2.95, -10.9) * mm, "end": v(-2.95, -3.5) * mm});
            skSolve(sketch);
        }
        {
            var Q0;
            Q0 = qSketchRegion(id + "F34", true);
            var Q1;
            {var subQ5=sQuery(id+"F34.wireOp",EDGE,"E111.0");Q1=makeQuery(id+"F34.imprint","IMPRINT",FACE,{"disambiguationData":[TD([[makeQuery(id+"F34.imprint","IMPRINT",EDGE,{"derivedFrom":subQ5}),1.0]])]});}
            extrude(context, id + "F35", {"entities" : qUnion([Q0, Q1]), "operationType" : NewBodyOperationType.REMOVE, "oppositeDirection" : true, "depth" : 1.5 * mm, "offsetDistance" : 25 * mm});
        }
        {
            var Q0;
            {var subQ0=sQuery(id+"F0.wireOp",EDGE,"E32.7");var subQ1=sQuery(id+"F0.wireOp",EDGE,"E30.filletArc");var subQ2=sQuery(id+"F0.wireOp",EDGE,"E32.5");var subQ3=sQuery(id+"F0.wireOp",EDGE,"E32.6");var subQ4=sQuery(id+"F0.wireOp",EDGE,"E27.right");var subQ5=sQuery(id+"F0.wireOp",EDGE,"E27.top");Q0=makeQuery(id+"F7.boolean.opBoolean","SPLIT",FACE,{"disambiguationData":[TD([makeQuery(id+"F1.opExtrude","SWEPT_FACE",FACE,{"disambiguationData":[OSD([subQ3])]})])],"derivedFrom":makeQuery(id+"F2.opExtrude","CAP_FACE",FACE,{"disambiguationData":[OSD([sQuery(id+"F0.wireOp",EDGE,"E27.bottom"),subQ5,sQuery(id+"F0.wireOp",EDGE,"E27.left"),subQ4,sQuery(id+"F0.wireOp",EDGE,"E28.filletArc"),sQuery(id+"F0.wireOp",EDGE,"E29.filletArc"),subQ1,sQuery(id+"F0.wireOp",EDGE,"E31.filletArc"),sQuery(id+"F0.wireOp",EDGE,"E32.0"),sQuery(id+"F0.wireOp",EDGE,"E32.1"),sQuery(id+"F0.wireOp",EDGE,"E32.2"),sQuery(id+"F0.wireOp",EDGE,"E32.3"),sQuery(id+"F0.wireOp",EDGE,"E32.4"),subQ2,subQ3,subQ0])],"isStart":false})});}
            var sketch = newSketch(context, id + "F36", { "sketchPlane" : qUnion([Q0])});
            skLineSegment(sketch, "E133.0", {"start": v(68.45, 6) * mm, "end": v(68.45, 3.5) * mm});
            skSolve(sketch);
        }
        {
            var Q0;
            Q0=makeQuery(id+"F36.imprint","IMPRINT",FACE,{"disambiguationData":[TD([[makeQuery(id+"F36.imprint","IMPRINT",EDGE,{"derivedFrom":sQuery(id+"F36.wireOp",EDGE,"E133.0")}),-1.0]])]});
            var sketch = newSketch(context, id + "F37", { "sketchPlane" : qUnion([Q0])});
            skLineSegment(sketch, "E134.0", {"start": v(68.45, 6) * mm, "end": v(68.45, 3.5) * mm});
            skArc(sketch, "E135.0", {"start": v(62, -2.95) * mm, "mid": v(66.56, -1.06) * mm, "end": v(68.45, 3.5) * mm});
            skLineSegment(sketch, "E136.0", {"start": v(58, -2.95) * mm, "end": v(62, -2.95) * mm});
            skLineSegment(sketch, "E137.0", {"start": v(45.4, -2.95) * mm, "end": v(50, -2.95) * mm});
            skLineSegment(sketch, "E138.0", {"start": v(17.9, -2.95) * mm, "end": v(37.4, -2.95) * mm});
            skLineSegment(sketch, "E139.0", {"start": v(3.5, -2.95) * mm, "end": v(6.9, -2.95) * mm});
            skArc(sketch, "E140.0", {"start": v(-2.95, 3.5) * mm, "mid": v(-1.06, -1.06) * mm, "end": v(3.5, -2.95) * mm});
            skLineSegment(sketch, "E141.0", {"start": v(-2.95, 10.9) * mm, "end": v(-2.95, 3.5) * mm});
            skLineSegment(sketch, "E142.0", {"start": v(-2.95, 26.5) * mm, "end": v(-2.95, 22.9) * mm});
            skArc(sketch, "E143.0", {"start": v(3.5, 32.95) * mm, "mid": v(-1.06, 31.06) * mm, "end": v(-2.95, 26.5) * mm});
            skLineSegment(sketch, "E144.0", {"start": v(3.5, 32.95) * mm, "end": v(62, 32.95) * mm});
            skArc(sketch, "E145.0", {"start": v(68.45, 26.5) * mm, "mid": v(66.56, 31.06) * mm, "end": v(62, 32.95) * mm});
            skLineSegment(sketch, "E146.0", {"start": v(68.45, 26.5) * mm, "end": v(68.45, 24) * mm});
            skLineSegment(sketch, "E147.0", {"start": v(67.4, 26.5) * mm, "end": v(67.4, 24) * mm});
            skLineSegment(sketch, "E147.1", {"start": v(-1.9, 26.5) * mm, "end": v(-1.9, 22.9) * mm});
            skArc(sketch, "E147.2", {"start": v(3.5, 31.9) * mm, "mid": v(-0.32, 30.32) * mm, "end": v(-1.9, 26.5) * mm});
            skLineSegment(sketch, "E147.3", {"start": v(3.5, 31.9) * mm, "end": v(62, 31.9) * mm});
            skArc(sketch, "E147.4", {"start": v(67.4, 26.5) * mm, "mid": v(65.82, 30.32) * mm, "end": v(62, 31.9) * mm});
            skLineSegment(sketch, "E148", {"start": v(68.45, 24) * mm, "end": v(67.4, 24) * mm});
            skLineSegment(sketch, "E149.0", {"start": v(66, 24) * mm, "end": v(68.45, 24) * mm});
            skLineSegment(sketch, "E150.0", {"start": v(-2.95, 22.9) * mm, "end": v(-0.5, 22.9) * mm});
            skLineSegment(sketch, "E151.0", {"start": v(-2.95, 10.9) * mm, "end": v(-0.5, 10.9) * mm});
            skLineSegment(sketch, "E152.0", {"start": v(6.9, -2.95) * mm, "end": v(6.9, -0.5) * mm});
            skLineSegment(sketch, "E153.0", {"start": v(3.5, -1.9) * mm, "end": v(6.9, -1.9) * mm});
            skArc(sketch, "E153.1", {"start": v(-1.9, 3.5) * mm, "mid": v(-0.32, -0.32) * mm, "end": v(3.5, -1.9) * mm});
            skLineSegment(sketch, "E153.2", {"start": v(-1.9, 10.9) * mm, "end": v(-1.9, 3.5) * mm});
            skLineSegment(sketch, "E154.bottom", {"start": v(37.4, -2.95) * mm, "end": v(17.9, -2.95) * mm});
            skLineSegment(sketch, "E154.top", {"start": v(37.4, -1.9) * mm, "end": v(17.9, -1.9) * mm});
            skLineSegment(sketch, "E154.left", {"start": v(37.4, -2.95) * mm, "end": v(37.4, -1.9) * mm});
            skLineSegment(sketch, "E154.right", {"start": v(17.9, -2.95) * mm, "end": v(17.9, -1.9) * mm});
            skLineSegment(sketch, "E155.bottom", {"start": v(50, -1.9) * mm, "end": v(45.4, -1.9) * mm});
            skLineSegment(sketch, "E155.top", {"start": v(50, -2.95) * mm, "end": v(45.4, -2.95) * mm});
            skLineSegment(sketch, "E155.left", {"start": v(50, -1.9) * mm, "end": v(50, -2.95) * mm});
            skLineSegment(sketch, "E155.right", {"start": v(45.4, -1.9) * mm, "end": v(45.4, -2.95) * mm});
            skLineSegment(sketch, "E156.0", {"start": v(67.4, 6) * mm, "end": v(67.4, 3.5) * mm});
            skArc(sketch, "E156.1", {"start": v(62, -1.9) * mm, "mid": v(65.82, -0.32) * mm, "end": v(67.4, 3.5) * mm});
            skLineSegment(sketch, "E156.2", {"start": v(58, -1.9) * mm, "end": v(62, -1.9) * mm});
            skLineSegment(sketch, "E157.0", {"start": v(66, 6) * mm, "end": v(68.45, 6) * mm});
            skLineSegment(sketch, "E158", {"start": v(58, -1.9) * mm, "end": v(58, -2.95) * mm});
            skLineSegment(sketch, "E159", {"start": v(68.45, 6) * mm, "end": v(67.4, 6) * mm});
            skSolve(sketch);
        }
        {
            var Q0;
            Q0 = qSketchRegion(id + "F37", true);
            extrude(context, id + "F38", {"entities" : qUnion([Q0]), "operationType" : NewBodyOperationType.ADD, "depth" : 1.5 * mm, "offsetDistance" : 25 * mm});
        }
        {
            var Q0;
            Q0=makeQuery(id+"F7.boolean.opBoolean","COPY",EDGE,{"derivedFrom":makeQuery(id+"F7.opExtrude","CAP_EDGE",EDGE,{"disambiguationData":[OSD([sQuery(id+"F6.wireOp",EDGE,"E42.right")])],"isStart":true})});
            var Q1;
            Q1=makeQuery(id+"F7.boolean.opBoolean","COPY",EDGE,{"derivedFrom":makeQuery(id+"F7.opExtrude","CAP_EDGE",EDGE,{"disambiguationData":[OSD([sQuery(id+"F6.wireOp",EDGE,"E42.left")])],"isStart":true})});
            chamfer(context, id + "F39", {"entities" : qUnion([Q0, Q1]), "width" : 1 * mm, "tangentPropagation" : true});
        }
        {
            var Q0;
            {var subQ0=sQuery(id+"F0.wireOp",EDGE,"E32.7");Q0=makeQuery(id+"F38.boolean.opBoolean","MERGE",FACE,{"derivedFrom":[makeQuery(id+"F2.boolean.opBoolean","MERGE",FACE,{"derivedFrom":[makeQuery(id+"F1.opExtrude","SWEPT_FACE",FACE,{"disambiguationData":[OSD([subQ0])]}),makeQuery(id+"F2.opExtrude","SWEPT_FACE",FACE,{"disambiguationData":[OSD([subQ0])]})]}),makeQuery(id+"F38.opExtrude","SWEPT_FACE",FACE,{"disambiguationData":[OSD([sQuery(id+"F37.wireOp",EDGE,"E136.0")])]}),makeQuery(id+"F38.opExtrude","SWEPT_FACE",FACE,{"disambiguationData":[OSD([sQuery(id+"F37.wireOp",EDGE,"E139.0")])]}),makeQuery(id+"F38.opExtrude","SWEPT_FACE",FACE,{"disambiguationData":[OSD([sQuery(id+"F37.wireOp",EDGE,"E154.bottom")])]}),makeQuery(id+"F38.opExtrude","SWEPT_FACE",FACE,{"disambiguationData":[OSD([sQuery(id+"F37.wireOp",EDGE,"E155.top")])]})]});}
            var sketch = newSketch(context, id + "F40", { "sketchPlane" : qUnion([Q0])});
            skPoint(sketch, "E160.0", {"position": v(37.4, 24) * mm});
            skPoint(sketch, "E161.0", {"position": v(45.4, 24) * mm});
            skLineSegment(sketch, "E162.bottom", {"start": v(35.9, 27) * mm, "end": v(46.9, 27) * mm});
            skLineSegment(sketch, "E162.top", {"start": v(35.9, 23.5) * mm, "end": v(46.9, 23.5) * mm});
            skLineSegment(sketch, "E162.left", {"start": v(35.9, 27) * mm, "end": v(35.9, 23.5) * mm});
            skLineSegment(sketch, "E162.right", {"start": v(46.9, 27) * mm, "end": v(46.9, 23.5) * mm});
            skPoint(sketch, "E163", {"position": v(41.4, 23.5) * mm});
            skLineSegment(sketch, "E164.0", {"start": v(37.9, 24.5) * mm, "end": v(44.9, 24.5) * mm});
            skPoint(sketch, "E165", {"position": v(41.4, 24.5) * mm});
            skLineSegment(sketch, "E166", {"start": v(41.4, 24.5) * mm, "end": v(41.4, 20.83) * mm, "construction": true});
            skLineSegment(sketch, "E167.bottom", {"start": v(48.5, 27) * mm, "end": v(59.5, 27) * mm});
            skLineSegment(sketch, "E167.top", {"start": v(48.5, 23.5) * mm, "end": v(59.5, 23.5) * mm});
            skLineSegment(sketch, "E167.left", {"start": v(48.5, 27) * mm, "end": v(48.5, 23.5) * mm});
            skLineSegment(sketch, "E167.right", {"start": v(59.5, 27) * mm, "end": v(59.5, 23.5) * mm});
            skPoint(sketch, "E168", {"position": v(54, 23.5) * mm});
            skLineSegment(sketch, "E169.0", {"start": v(50.5, 24.5) * mm, "end": v(57.5, 24.5) * mm});
            skLineSegment(sketch, "E170", {"start": v(54, 24.5) * mm, "end": v(54, 21.91) * mm, "construction": true});
            skLineSegment(sketch, "E171.0", {"start": v(6.9, 24) * mm, "end": v(17.9, 24) * mm});
            skLineSegment(sketch, "E172", {"start": v(12.4, 24) * mm, "end": v(12.4, 20.7) * mm, "construction": true});
            skLineSegment(sketch, "E173.bottom", {"start": v(2.9, 27) * mm, "end": v(21.9, 27) * mm});
            skLineSegment(sketch, "E173.top", {"start": v(2.9, 23.5) * mm, "end": v(21.9, 23.5) * mm});
            skLineSegment(sketch, "E173.left", {"start": v(2.9, 27) * mm, "end": v(2.9, 23.5) * mm});
            skLineSegment(sketch, "E173.right", {"start": v(21.9, 27) * mm, "end": v(21.9, 23.5) * mm});
            skPoint(sketch, "E174", {"position": v(12.4, 23.5) * mm});
            skSolve(sketch);
        }
        {
            var Q0;
            Q0 = qSketchRegion(id + "F40", true);
            var Q1;
            Q1=makeQuery(id+"F35.boolean.opBoolean","COPY",FACE,{"derivedFrom":makeQuery(id+"F35.opExtrude","SWEPT_FACE",FACE,{"disambiguationData":[OSD([sQuery(id+"F34.wireOp",EDGE,"E115.top")])]})});
            extrude(context, id + "F41", {"entities" : qUnion([Q0]), "operationType" : NewBodyOperationType.REMOVE, "endBound" : BoundingType.UP_TO_SURFACE, "oppositeDirection" : true, "depth" : 25 * mm, "endBoundEntityFace" : qUnion([Q1]), "offsetDistance" : 25 * mm});
        }
        {
            var Q0;
            {var subQ0=sQuery(id+"F0.wireOp",EDGE,"E32.7");Q0=makeQuery(id+"F38.boolean.opBoolean","MERGE",FACE,{"derivedFrom":[makeQuery(id+"F2.boolean.opBoolean","MERGE",FACE,{"derivedFrom":[makeQuery(id+"F1.opExtrude","SWEPT_FACE",FACE,{"disambiguationData":[OSD([subQ0])]}),makeQuery(id+"F2.opExtrude","SWEPT_FACE",FACE,{"disambiguationData":[OSD([subQ0])]})]}),makeQuery(id+"F38.opExtrude","SWEPT_FACE",FACE,{"disambiguationData":[OSD([sQuery(id+"F37.wireOp",EDGE,"E136.0")])]}),makeQuery(id+"F38.opExtrude","SWEPT_FACE",FACE,{"disambiguationData":[OSD([sQuery(id+"F37.wireOp",EDGE,"E139.0")])]}),makeQuery(id+"F38.opExtrude","SWEPT_FACE",FACE,{"disambiguationData":[OSD([sQuery(id+"F37.wireOp",EDGE,"E154.bottom")])]}),makeQuery(id+"F38.opExtrude","SWEPT_FACE",FACE,{"disambiguationData":[OSD([sQuery(id+"F37.wireOp",EDGE,"E155.top")])]})]});}
            var sketch = newSketch(context, id + "F42", { "sketchPlane" : qUnion([Q0])});
            skLineSegment(sketch, "E175.0", {"start": v(51.25, 1.75) * mm, "end": v(56.75, 1.75) * mm});
            skLineSegment(sketch, "E176.0", {"start": v(38.65, 1.75) * mm, "end": v(44.15, 1.75) * mm});
            skLineSegment(sketch, "E177", {"start": v(54, 1.75) * mm, "end": v(54, 10.35) * mm, "construction": true});
            skLineSegment(sketch, "E178", {"start": v(41.4, 1.75) * mm, "end": v(41.4, 8.14) * mm, "construction": true});
            skLineSegment(sketch, "E179.bottom", {"start": v(59.5, -2) * mm, "end": v(48.5, -2) * mm});
            skLineSegment(sketch, "E179.top", {"start": v(59.5, 4.75) * mm, "end": v(48.5, 4.75) * mm});
            skLineSegment(sketch, "E179.left", {"start": v(59.5, -2) * mm, "end": v(59.5, 4.75) * mm});
            skLineSegment(sketch, "E179.right", {"start": v(48.5, -2) * mm, "end": v(48.5, 4.75) * mm});
            skLineSegment(sketch, "E180.bottom", {"start": v(46.9, -2) * mm, "end": v(35.9, -2) * mm});
            skLineSegment(sketch, "E180.top", {"start": v(46.9, 4.75) * mm, "end": v(35.9, 4.75) * mm});
            skLineSegment(sketch, "E180.left", {"start": v(46.9, -2) * mm, "end": v(46.9, 4.75) * mm});
            skLineSegment(sketch, "E180.right", {"start": v(35.9, -2) * mm, "end": v(35.9, 4.75) * mm});
            skPoint(sketch, "E181", {"position": v(41.4, 4.75) * mm});
            skPoint(sketch, "E182", {"position": v(54, 4.75) * mm});
            skLineSegment(sketch, "E183.0", {"start": v(7.9, 2.25) * mm, "end": v(16.9, 2.25) * mm});
            skLineSegment(sketch, "E184", {"start": v(12.4, 2.25) * mm, "end": v(12.4, 8.8) * mm, "construction": true});
            skLineSegment(sketch, "E185.bottom", {"start": v(2.9, -2) * mm, "end": v(21.9, -2) * mm});
            skLineSegment(sketch, "E185.top", {"start": v(2.9, 4.75) * mm, "end": v(21.9, 4.75) * mm});
            skLineSegment(sketch, "E185.left", {"start": v(2.9, -2) * mm, "end": v(2.9, 4.75) * mm});
            skLineSegment(sketch, "E185.right", {"start": v(21.9, -2) * mm, "end": v(21.9, 4.75) * mm});
            skPoint(sketch, "E186", {"position": v(12.4, 4.75) * mm});
            skSolve(sketch);
        }
        {
            var Q0;
            Q0 = qSketchRegion(id + "F42", true);
            var Q1;
            Q1=makeQuery(id+"F38.opExtrude","SWEPT_FACE",FACE,{"disambiguationData":[OSD([sQuery(id+"F37.wireOp",EDGE,"E155.bottom")])]});
            extrude(context, id + "F43", {"entities" : qUnion([Q0]), "operationType" : NewBodyOperationType.REMOVE, "endBound" : BoundingType.UP_TO_SURFACE, "oppositeDirection" : true, "depth" : 25 * mm, "endBoundEntityFace" : qUnion([Q1]), "offsetDistance" : 25 * mm});
        }
    });
